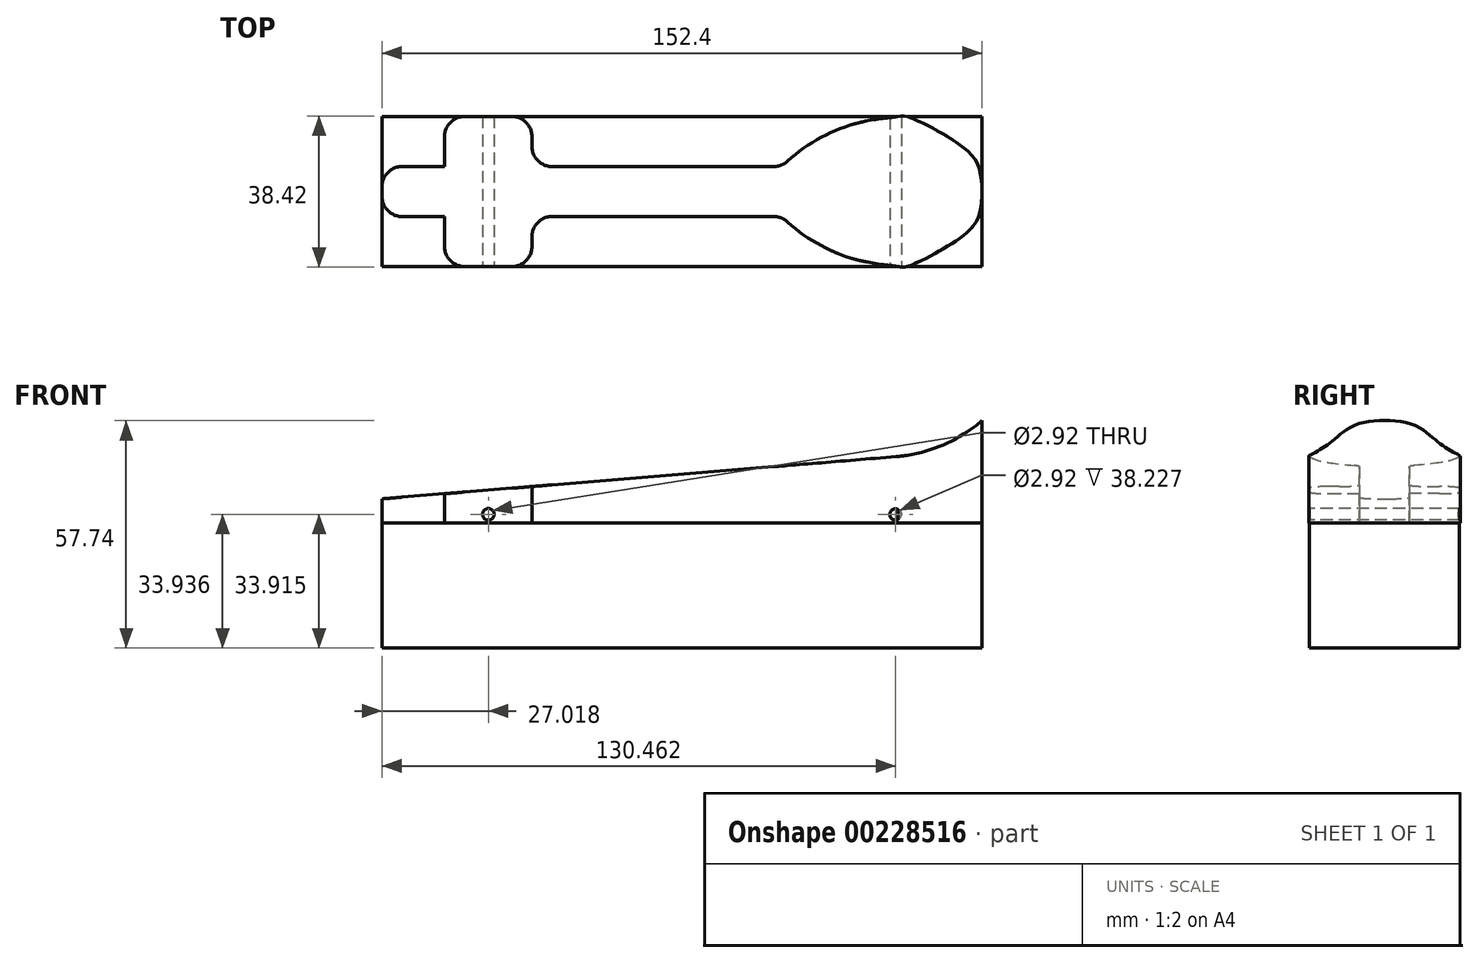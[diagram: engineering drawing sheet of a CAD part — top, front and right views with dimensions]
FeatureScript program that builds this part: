
annotation { "Feature Type Name" : "Feature", "Feature Type Description" : "" }
export const myFeature = defineFeature(function(context is Context, id is Id, definition is map)
    precondition{}
    {
        {
            var Q0;
            Q0=qCreatedBy(makeId("Top.planeOp"),FACE);
            var sketch = newSketch(context, id + "F0", { "sketchPlane" : qUnion([Q0])});
            skLineSegment(sketch, "E0.bottom", {"start": v(-76.2, 19.05) * mm, "end": v(76.2, 19.05) * mm});
            skLineSegment(sketch, "E0.top", {"start": v(-76.2, -19.05) * mm, "end": v(76.2, -19.05) * mm});
            skLineSegment(sketch, "E0.left", {"start": v(-76.2, 19.05) * mm, "end": v(-76.2, -19.05) * mm});
            skLineSegment(sketch, "E0.right", {"start": v(76.2, 19.05) * mm, "end": v(76.2, -19.05) * mm});
            skPoint(sketch, "E0.middle", {"position": v(0, 0) * mm});
            skSolve(sketch);
        }
        {
            var Q0;
            Q0=makeQuery(id+"F0.imprint","IMPRINT",FACE,{"disambiguationData":[TD([[makeQuery(id+"F0.imprint","IMPRINT",EDGE,{"derivedFrom":sQuery(id+"F0.wireOp",EDGE,"E0.bottom")}),-1.0]])]});
            extrude(context, id + "F1", {"entities" : qUnion([Q0]), "depth" : 31.75 * mm});
        }
        {
            var Q0;
            Q0=makeQuery(id+"F1.opExtrude","CAP_FACE",FACE,{"disambiguationData":[OSD([sQuery(id+"F0.wireOp",EDGE,"E0.bottom"),sQuery(id+"F0.wireOp",EDGE,"E0.top"),sQuery(id+"F0.wireOp",EDGE,"E0.left"),sQuery(id+"F0.wireOp",EDGE,"E0.right")])],"isStart":false});
            var sketch = newSketch(context, id + "F2", { "sketchPlane" : qUnion([Q0])});
            skLineSegment(sketch, "E1", {"start": v(-76.2, -6.35) * mm, "end": v(-60.33, -6.35) * mm});
            skLineSegment(sketch, "E2", {"start": v(-76.2, -6.35) * mm, "end": v(-76.2, 0) * mm});
            skLineSegment(sketch, "E3", {"start": v(-60.33, -6.35) * mm, "end": v(-60.33, -19.05) * mm});
            skLineSegment(sketch, "E4", {"start": v(-60.33, -19.05) * mm, "end": v(-38.1, -19.05) * mm});
            skLineSegment(sketch, "E5", {"start": v(-38.1, -19.05) * mm, "end": v(-38.1, -6.35) * mm});
            skLineSegment(sketch, "E6", {"start": v(-38.1, -6.35) * mm, "end": v(25.4, -6.35) * mm});
            skLineSegment(sketch, "E7.MirrorCS", {"start": v(-76.2, 6.35) * mm, "end": v(-60.33, 6.35) * mm});
            skLineSegment(sketch, "E8.MirrorCS", {"start": v(-60.33, 19.05) * mm, "end": v(-38.1, 19.05) * mm});
            skLineSegment(sketch, "E9.MirrorCS", {"start": v(-60.33, 6.35) * mm, "end": v(-60.33, 19.05) * mm});
            skLineSegment(sketch, "E10.MirrorCS", {"start": v(-38.1, 19.05) * mm, "end": v(-38.1, 6.35) * mm});
            skLineSegment(sketch, "E11.MirrorCS", {"start": v(-38.1, 6.35) * mm, "end": v(25.4, 6.35) * mm});
            skLineSegment(sketch, "E12.MirrorCS", {"start": v(-76.2, 6.35) * mm, "end": v(-76.2, 0) * mm});
            skFitSpline(sketch, "E13", {"points": [v(25.4, -6.35) * mm, v(43.53, -17.1) * mm, v(54.93, -19.05) * mm, v(57.18, -19.05) * mm, v(70.28, -12.1) * mm, v(75.35, -6.35) * mm, v(76.2, 0) * mm], "startDerivative": vector(58.47, -60.37) * mm, "endDerivative": vector(0, 45.15) * mm});
            skFitSpline(sketch, "E14.MirrorCS", {"points": [v(25.4, 6.35) * mm, v(43.53, 17.1) * mm, v(54.93, 19.05) * mm, v(57.18, 19.05) * mm, v(70.28, 12.1) * mm, v(75.35, 6.35) * mm, v(76.2, 0) * mm], "startDerivative": vector(58.47, 60.37) * mm, "endDerivative": vector(0, -45.15) * mm});
            skLineSegment(sketch, "E15", {"start": v(76.2, -19.05) * mm, "end": v(57.18, -19.05) * mm});
            skSolve(sketch);
        }
        {
            var Q0;
            Q0 = qSketchRegion(id + "F2", true);
            extrude(context, id + "F3", {"entities" : qUnion([Q0]), "depth" : 28.57 * mm});
        }
        {
            var Q0;
            Q0=makeQuery(id+"F3.opExtrude","SWEPT_EDGE",EDGE,{"disambiguationData":[OSD([sQuery(id+"F0.wireOp",EDGE,"E0.left"),sQuery(id+"F2.wireOp",EDGE,"E1"),sQuery(id+"F2.wireOp",EDGE,"E2")])]});
            var Q1;
            Q1=makeQuery(id+"F3.opExtrude","SWEPT_EDGE",EDGE,{"disambiguationData":[OSD([sQuery(id+"F0.wireOp",EDGE,"E0.top"),sQuery(id+"F2.wireOp",EDGE,"E3"),sQuery(id+"F2.wireOp",EDGE,"E4")])]});
            var Q2;
            Q2=makeQuery(id+"F3.opExtrude","SWEPT_EDGE",EDGE,{"disambiguationData":[OSD([sQuery(id+"F0.wireOp",EDGE,"E0.top"),sQuery(id+"F2.wireOp",EDGE,"E4"),sQuery(id+"F2.wireOp",EDGE,"E5")])]});
            var Q3;
            Q3=makeQuery(id+"F3.opExtrude","SWEPT_EDGE",EDGE,{"disambiguationData":[OSD([sQuery(id+"F2.wireOp",EDGE,"E5"),sQuery(id+"F2.wireOp",EDGE,"E6")])]});
            var Q4;
            Q4=makeQuery(id+"F3.opExtrude","SWEPT_EDGE",EDGE,{"disambiguationData":[OSD([sQuery(id+"F2.wireOp",EDGE,"E6"),sQuery(id+"F2.wireOp",EDGE,"5440ff07-c519-4c66-a4cc-310d62306805")])]});
            var Q5;
            Q5=makeQuery(id+"F3.opExtrude","SWEPT_EDGE",EDGE,{"disambiguationData":[OSD([sQuery(id+"F0.wireOp",EDGE,"E0.right"),sQuery(id+"F2.wireOp",EDGE,"5440ff07-c519-4c66-a4cc-310d62306805"),sQuery(id+"F2.wireOp",EDGE,"4cf1e881-b031-4800-91a2-0e4df43e7d430.MirrorCS")])]});
            fillet(context, id + "F4", {"entities" : qUnion([Q0, Q1, Q2, Q3, Q4, Q5]), "radius" : 5.08 * mm, "tangentPropagation" : true, "allowEdgeOverflow" : false});
        }
        {
            var Q0;
            Q0=makeQuery(id+"F3.opExtrude","SWEPT_EDGE",EDGE,{"disambiguationData":[OSD([sQuery(id+"F0.wireOp",EDGE,"E0.left"),sQuery(id+"F2.wireOp",EDGE,"E7.MirrorCS"),sQuery(id+"F2.wireOp",EDGE,"E12.MirrorCS")])]});
            var Q1;
            Q1=makeQuery(id+"F3.opExtrude","SWEPT_EDGE",EDGE,{"disambiguationData":[OSD([sQuery(id+"F0.wireOp",EDGE,"E0.bottom"),sQuery(id+"F2.wireOp",EDGE,"E8.MirrorCS"),sQuery(id+"F2.wireOp",EDGE,"E10.MirrorCS")])]});
            var Q2;
            Q2=makeQuery(id+"F3.opExtrude","SWEPT_EDGE",EDGE,{"disambiguationData":[OSD([sQuery(id+"F0.wireOp",EDGE,"E0.bottom"),sQuery(id+"F2.wireOp",EDGE,"E8.MirrorCS"),sQuery(id+"F2.wireOp",EDGE,"E9.MirrorCS")])]});
            var Q3;
            Q3=makeQuery(id+"F3.opExtrude","SWEPT_EDGE",EDGE,{"disambiguationData":[OSD([sQuery(id+"F2.wireOp",EDGE,"E11.MirrorCS"),sQuery(id+"F2.wireOp",EDGE,"4cf1e881-b031-4800-91a2-0e4df43e7d430.MirrorCS")])]});
            var Q4;
            Q4=makeQuery(id+"F3.opExtrude","SWEPT_EDGE",EDGE,{"disambiguationData":[OSD([sQuery(id+"F2.wireOp",EDGE,"E10.MirrorCS"),sQuery(id+"F2.wireOp",EDGE,"E11.MirrorCS")])]});
            var Q5;
            {var subQ0=sQuery(id+"F2.wireOp",EDGE,"4cf1e881-b031-4800-91a2-0e4df43e7d430.MirrorCS");var subQ1=sQuery(id+"F2.wireOp",EDGE,"5440ff07-c519-4c66-a4cc-310d62306805");var subQ2=sQuery(id+"F0.wireOp",EDGE,"E0.right");var subQ3=makeQuery(id+"F1.opExtrude","CAP_EDGE",EDGE,{"disambiguationData":[OSD([sQuery(id+"F0.wireOp",EDGE,"E0.bottom")])],"isStart":false});var subQ4=makeQuery(id+"F2.imprint","INTERSECT",VERTEX,{"disambiguationData":[OD(1.0)],"derivedFrom":[subQ3,subQ0]});var subQ5=makeQuery(id+"F2.imprint","INTERSECT",VERTEX,{"disambiguationData":[OD(0.0)],"derivedFrom":[subQ3,subQ0]});Q5=makeQuery(id+"F4.opFillet","BLEND_EDGE",EDGE,{"blendedFrom":[makeQuery(id+"F3.opExtrude","SWEPT_EDGE",EDGE,{"disambiguationData":[OSD([subQ2,subQ1,subQ0])]}),makeQuery(id+"F3.opExtrude","SWEPT_FACE",FACE,{"disambiguationData":[OSD([subQ0]),TDD([makeQuery(id+"F2.imprint","IMPRINT",EDGE,{"disambiguationData":[TD([[makeQuery(id+"F2.imprint","INTERSECT",VERTEX,{"disambiguationData":[OD(1.0)],"derivedFrom":[sQuery(id+"F2.wireOp",EDGE,"97941c5f-bdcf-44d4-9933-6ee6f42daaee0.MirrorCS"),subQ0]}),-1.0]])],"derivedFrom":subQ0}),makeQuery(id+"F2.imprint","IMPRINT",EDGE,{"disambiguationData":[TD([[subQ5,-1.0]])],"derivedFrom":subQ0}),makeQuery(id+"F2.imprint","IMPRINT",EDGE,{"disambiguationData":[TD([[subQ4,-1.0]])],"derivedFrom":subQ0})])]})],"blendedInto":[makeQuery(id+"F3.opExtrude","SWEPT_FACE",FACE,{"disambiguationData":[OSD([subQ0]),TDD([makeQuery(id+"F2.imprint","IMPRINT",EDGE,{"disambiguationData":[TD([[makeQuery(id+"F2.imprint","INTERSECT",VERTEX,{"disambiguationData":[OD(1.0)],"derivedFrom":[sQuery(id+"F2.wireOp",EDGE,"97941c5f-bdcf-44d4-9933-6ee6f42daaee0.MirrorCS"),subQ0]}),-1.0]])],"derivedFrom":subQ0}),makeQuery(id+"F2.imprint","IMPRINT",EDGE,{"disambiguationData":[TD([[subQ5,-1.0]])],"derivedFrom":subQ0}),makeQuery(id+"F2.imprint","IMPRINT",EDGE,{"disambiguationData":[TD([[subQ4,-1.0]])],"derivedFrom":subQ0})])]})]});}
            fillet(context, id + "F5", {"entities" : qUnion([Q0, Q1, Q2, Q3, Q4, Q5]), "radius" : 5.08 * mm, "tangentPropagation" : true, "allowEdgeOverflow" : false});
        }
        {
            var Q0;
            Q0=qCreatedBy(makeId("Front.planeOp"),FACE);
            var sketch = newSketch(context, id + "F6", { "sketchPlane" : qUnion([Q0])});
            skLineSegment(sketch, "E16", {"start": v(-101.15, 29.68) * mm, "end": v(-101.15, 37.02) * mm, "construction": true});
            skLineSegment(sketch, "E17", {"start": v(-86.5, 37.02) * mm, "end": v(54.42, 48.6) * mm});
            skLineSegment(sketch, "E18", {"start": v(78.85, 60.26) * mm, "end": v(79.17, 60.6) * mm});
            skLineSegment(sketch, "E19", {"start": v(-86.5, 37.02) * mm, "end": v(-86.5, 62.42) * mm});
            skLineSegment(sketch, "E20", {"start": v(-86.5, 62.42) * mm, "end": v(79.17, 60.6) * mm});
            skPoint(sketch, "E21.visualSharp", {"position": v(68.85, 49.79) * mm});
            skArc(sketch, "E21.filletArc", {"start": v(54.42, 48.6) * mm, "mid": v(67.7, 52.19) * mm, "end": v(78.85, 60.26) * mm});
            skSolve(sketch);
        }
        {
            var Q0;
            Q0 = qSketchRegion(id + "F6", true);
            extrude(context, id + "F7", {"entities" : qUnion([Q0]), "operationType" : NewBodyOperationType.REMOVE, "oppositeDirection" : true, "depth" : 161.04 * mm, "symmetric" : true});
        }
        {
            var Q0;
            Q0=makeQuery(id+"F3.opExtrude","SWEPT_FACE",FACE,{"disambiguationData":[OSD([sQuery(id+"F2.wireOp",EDGE,"E4")])]});
            var sketch = newSketch(context, id + "F8", { "sketchPlane" : qUnion([Q0])});
            skCircle(sketch, "E22", {"center": v(-49.21, 31.75) * mm, "radius": 1.4 * mm});
            skSolve(sketch);
        }
        {
            var Q0;
            Q0=makeQuery(id+"F1.opExtrude","SWEPT_FACE",FACE,{"disambiguationData":[OSD([sQuery(id+"F0.wireOp",EDGE,"E0.top")])]});
            var sketch = newSketch(context, id + "F9", { "sketchPlane" : qUnion([Q0])});
            skCircle(sketch, "E23", {"center": v(54.23, 31.75) * mm, "radius": 1.4 * mm});
            skSolve(sketch);
        }
        {
            var Q0;
            {var subQ0=sQuery(id+"F2.wireOp",EDGE,"E4");var subQ1=makeQuery(id+"F3.opExtrude","SWEPT_FACE",FACE,{"disambiguationData":[OSD([subQ0])]});Q0=makeQuery(id+"F8.imprint","IMPRINT",FACE,{"disambiguationData":[TD([[makeQuery(id+"F8.imprint","IMPRINT",EDGE,{"derivedFrom":makeQuery(id+"F7.boolean.opBoolean","INTERSECT",EDGE,{"derivedFrom":[subQ1,makeQuery(id+"F7.opExtrude","SWEPT_FACE",FACE,{"disambiguationData":[OSD([sQuery(id+"F6.wireOp",EDGE,"E17")])]})]})}),1.0]])]});}
            var sketch = newSketch(context, id + "F10", { "sketchPlane" : qUnion([Q0])});
            skCircle(sketch, "E24", {"center": v(-49.18, 33.94) * mm, "radius": 1.46 * mm});
            skSolve(sketch);
        }
        {
            var Q0;
            {var subQ0=sQuery(id+"F0.wireOp",EDGE,"E0.top");Q0=makeQuery(id+"F9.imprint","IMPRINT",FACE,{"disambiguationData":[TD([[makeQuery(id+"F9.imprint","IMPRINT",EDGE,{"derivedFrom":makeQuery(id+"F1.opExtrude","CAP_EDGE",EDGE,{"disambiguationData":[OSD([subQ0])],"isStart":true})}),1.0]])]});}
            var sketch = newSketch(context, id + "F11", { "sketchPlane" : qUnion([Q0])});
            skCircle(sketch, "E25", {"center": v(54.26, 33.92) * mm, "radius": 1.46 * mm});
            skSolve(sketch);
        }
        {
            var Q0;
            Q0 = qSketchRegion(id + "F10", true);
            extrude(context, id + "F12", {"entities" : qUnion([Q0]), "operationType" : NewBodyOperationType.REMOVE, "endBound" : BoundingType.THROUGH_ALL, "oppositeDirection" : true, "depth" : 25.4 * mm});
        }
        {
            var Q0;
            Q0 = qSketchRegion(id + "F11", true);
            extrude(context, id + "F13", {"entities" : qUnion([Q0]), "operationType" : NewBodyOperationType.REMOVE, "endBound" : BoundingType.THROUGH_ALL, "oppositeDirection" : true, "depth" : 25.4 * mm});
        }
    });
